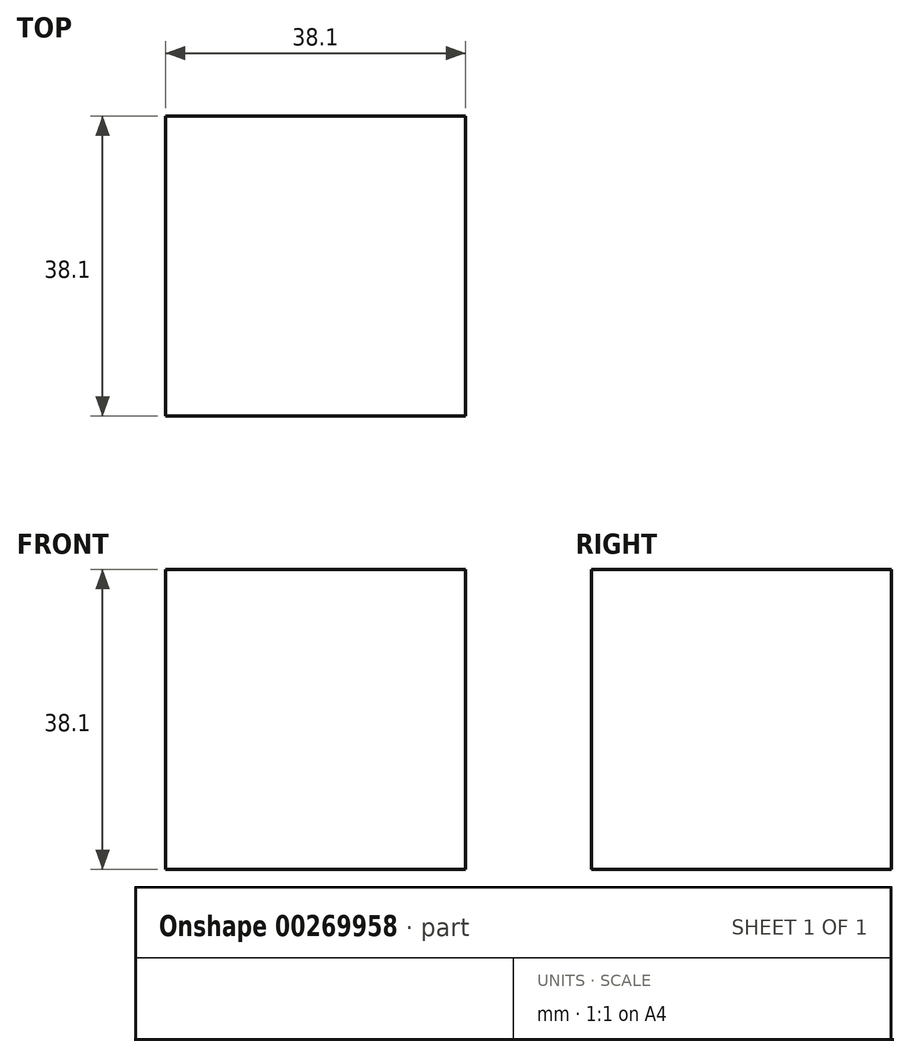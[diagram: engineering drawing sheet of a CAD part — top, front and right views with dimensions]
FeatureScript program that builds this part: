
annotation { "Feature Type Name" : "Feature", "Feature Type Description" : "" }
export const myFeature = defineFeature(function(context is Context, id is Id, definition is map)
    precondition{}
    {
        {
            var Q0;
            Q0=qCreatedBy(makeId("Top.planeOp"),FACE);
            var sketch = newSketch(context, id + "F0", { "sketchPlane" : qUnion([Q0])});
            skLineSegment(sketch, "E0.bottom", {"start": v(0, 0) * mm, "end": v(38.1, 0) * mm});
            skLineSegment(sketch, "E0.top", {"start": v(0, 38.1) * mm, "end": v(38.1, 38.1) * mm});
            skLineSegment(sketch, "E0.left", {"start": v(0, 0) * mm, "end": v(0, 38.1) * mm});
            skLineSegment(sketch, "E0.right", {"start": v(38.1, 0) * mm, "end": v(38.1, 38.1) * mm});
            skSolve(sketch);
        }
        {
            var Q0;
            Q0=makeQuery(id+"F0.imprint","IMPRINT",FACE,{"disambiguationData":[TD([[makeQuery(id+"F0.imprint","IMPRINT",EDGE,{"derivedFrom":sQuery(id+"F0.wireOp",EDGE,"E0.bottom")}),1.0]])]});
            extrude(context, id + "F1", {"entities" : qUnion([Q0]), "depth" : 38.1 * mm});
        }
    });
